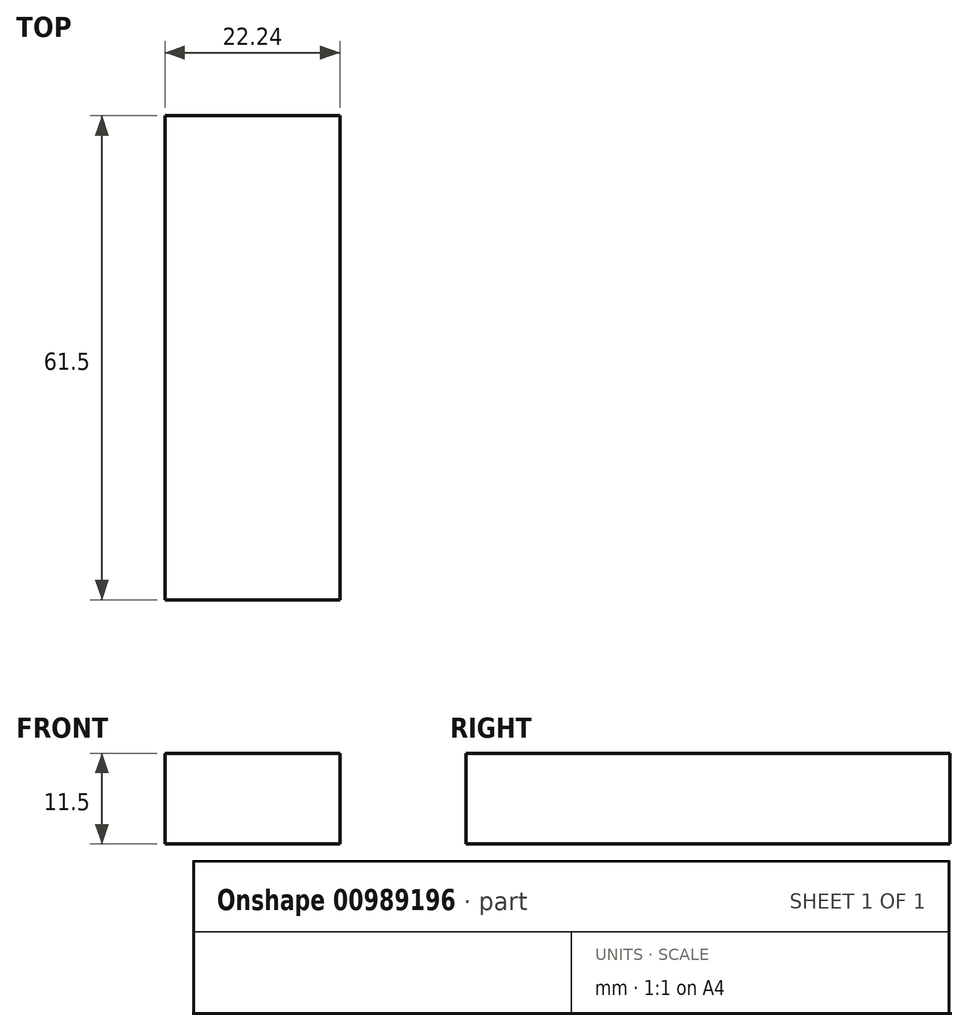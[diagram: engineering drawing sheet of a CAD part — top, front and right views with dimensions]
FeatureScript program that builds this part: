
annotation { "Feature Type Name" : "Feature", "Feature Type Description" : "" }
export const myFeature = defineFeature(function(context is Context, id is Id, definition is map)
    precondition{}
    {
        {
            var Q0;
            Q0=qCreatedBy(makeId("Top.planeOp"),FACE);
            cPlane(context, id + "F0", {"entities" : qUnion([Q0]), "cplaneType" : CPlaneType.OFFSET, "offset" : 12.45 * mm, "width" : 150 * mm, "height" : 150 * mm});
        }
        {
            var Q0;
            Q0=qCreatedBy(id+"F0.planeOp",FACE);
            var sketch = newSketch(context, id + "F1", { "sketchPlane" : qUnion([Q0])});
            skLineSegment(sketch, "E0.bottom", {"start": v(-5.12, -30.75) * mm, "end": v(-5.12, 30.75) * mm});
            skLineSegment(sketch, "E0.top", {"start": v(17.12, -30.75) * mm, "end": v(17.12, 30.75) * mm});
            skLineSegment(sketch, "E0.left", {"start": v(-5.12, -30.75) * mm, "end": v(17.12, -30.75) * mm});
            skLineSegment(sketch, "E0.right", {"start": v(-5.12, 30.75) * mm, "end": v(17.12, 30.75) * mm});
            skPoint(sketch, "E0.middle", {"position": v(6, 0) * mm});
            skLineSegment(sketch, "E1", {"start": v(6, 0) * mm, "end": v(0, 0) * mm, "construction": true});
            skLineSegment(sketch, "E2", {"start": v(6, 0) * mm, "end": v(6, 0) * mm});
            skSolve(sketch);
        }
        {
            var Q0;
            Q0=makeQuery(id+"F1.imprint","IMPRINT",FACE,{"disambiguationData":[TD([[makeQuery(id+"F1.imprint","IMPRINT",EDGE,{"derivedFrom":sQuery(id+"F1.wireOp",EDGE,"E0.bottom")}),-1.0]])]});
            extrude(context, id + "F2", {"entities" : qUnion([Q0]), "depth" : 11.5 * mm, "offsetDistance" : 25 * mm});
        }
    });
